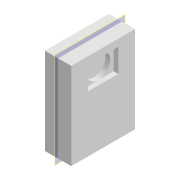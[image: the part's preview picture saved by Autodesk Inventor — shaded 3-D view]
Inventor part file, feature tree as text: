
AUTODESK INVENTOR PART (.ipt)
format: ipt  version: 2022 (Build 260153000, 153)  size: 116,736 bytes
history: native  units: mm
features: extrude x4, sketch x4, projected_geometry x3, plane x1
ambient origin geometry x8: Origin, YZ Plane, XZ Plane, XY Plane, X Axis, Y Axis, Z Axis, Center Point
bodies: Volumenkörper1 (feature_tree)
feature tree (12):
  extrude  "Extrusion1"  Depth=13.6mm
  extrude  "Extrusion2"  Depth=6.5mm
  extrude  "Extrusion3"  Depth=1.5mm
  extrude  "Extrusion4"  Depth=1.0mm TaperAngle=0.0deg
  plane  "Arbeitsebene1"
  sketch  "Skizze1"  dims[d0=18.5mm d1=13.6mm]
  sketch  "Skizze2"  dims[d2=5.6mm d3=0.0mm d4=6.5mm]
  projected_geometry  "Projizierte Kontur1"
  sketch  "Skizze3"  dims[d5=5.0mm d6=1.5mm]
  projected_geometry  "Projizierte Kontur2"
  sketch  "Skizze4"  dims[d7=1.0mm d8=0.0mm d9=1.0mm d10=0.0mm d11=1.0mm d12=0.0mm]
  projected_geometry  "Projizierte Kontur3"
